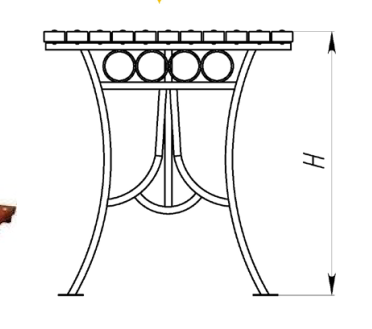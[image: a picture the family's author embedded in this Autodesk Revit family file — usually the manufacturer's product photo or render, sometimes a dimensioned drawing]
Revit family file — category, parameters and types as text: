
# Revit family: Стол садовый «Олимп» Арт 6697
name_source: partatom
category: Антураж
revit_build: Autodesk Revit 2018 (Build: 20180423_1000(x64)
units: mm (PartAtom-declared; Revit-internal decimal feet)

## family parameters
Всегда вертикально = Да
Источник визуального образа = Геометрия семейства
На основе рабочей плоскости = Нет
Общий = Нет
При загрузке вырезать с полостями = Нет
Точка расчета площади = Нет

## types (5) — shared parameters
URL = https://hobbyka.ru
Артикул товара = Арт. 6697
Высота = 760 мм
Группа модели = Садовые столы
Изготовитель = ООО «Хоббика»
Изображение типоразмера = Стол садовый «Олимп» Арт 6697.png
Материал изделия = Сталь, дерево
Цвет опор = Сталь
Цвет столешници = Дерево Тик
Ширина = 710 мм

## per-type parameters (varying)
| type | Версия 1,2 м | Версия 1,5 м | Версия 1,8 м | Версия 2,0 м | Версия 3,0 м | Длина | Описание |
| Модель 1,2 м | Да | Нет | Нет | Нет | Нет | 1200 мм | Стол садовый «Олимп» модель 1,2 м |
| Модель 1,5 м | Нет | Да | Нет | Нет | Нет | 1500 мм | Стол садовый «Олимп» модель 1,5 м |
| Модель 1,8 м | Нет | Нет | Да | Нет | Нет | 1800 мм | Стол садовый «Олимп» модель 1,8 м |
| Модель 2,0 м | Нет | Нет | Нет | Да | Нет | 2000 мм | Стол садовый «Олимп» модель 2,0 м |
| Модель 3,0 м | Нет | Нет | Нет | Нет | Да | 3000 мм | Стол садовый «Олимп» модель 3,0 м |
